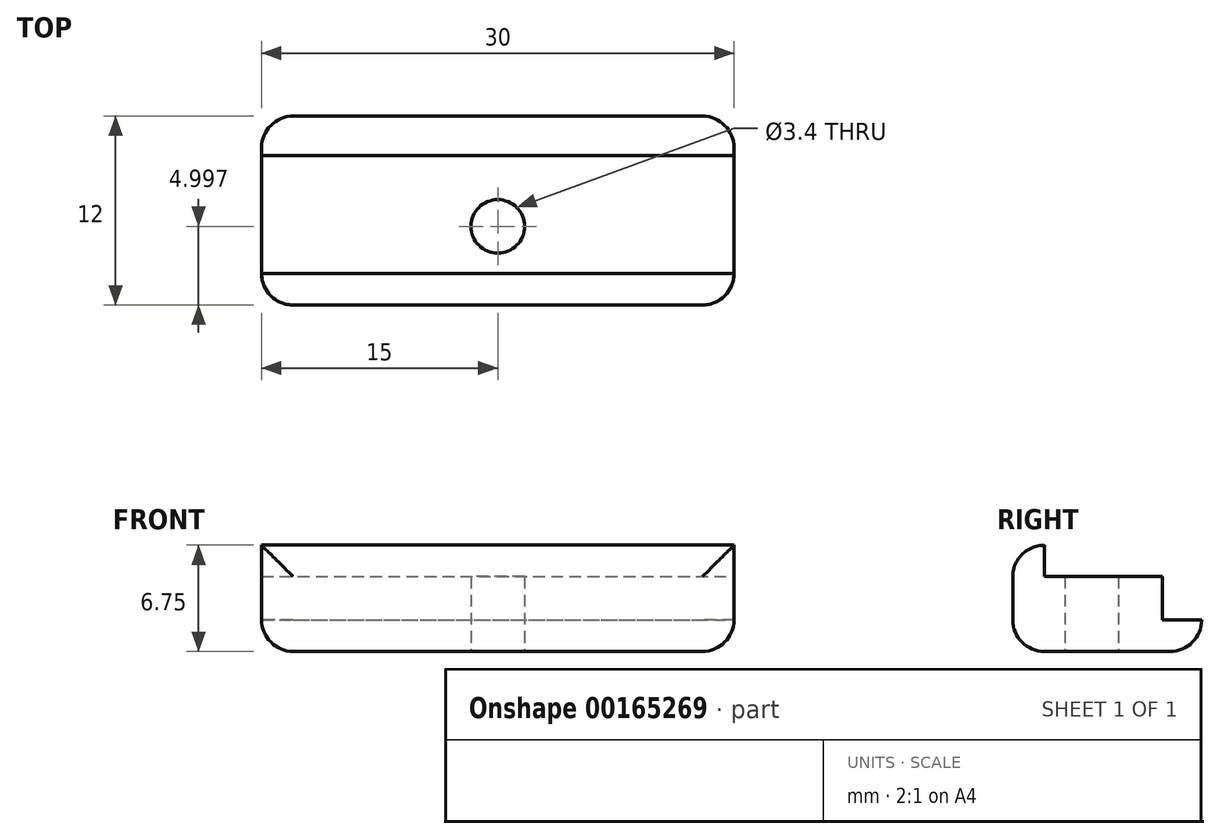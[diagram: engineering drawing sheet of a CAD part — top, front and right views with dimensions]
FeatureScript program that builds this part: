
annotation { "Feature Type Name" : "Feature", "Feature Type Description" : "" }
export const myFeature = defineFeature(function(context is Context, id is Id, definition is map)
    precondition{}
    {
        {
            var Q0;
            Q0=qCreatedBy(makeId("Top.planeOp"),FACE);
            var sketch = newSketch(context, id + "F0", { "sketchPlane" : qUnion([Q0])});
            skLineSegment(sketch, "E0.bottom", {"start": v(-7.16, 2.14) * mm, "end": v(22.84, 2.14) * mm});
            skLineSegment(sketch, "E0.top", {"start": v(-7.16, -9.86) * mm, "end": v(22.84, -9.86) * mm});
            skLineSegment(sketch, "E0.left", {"start": v(-7.16, 2.14) * mm, "end": v(-7.16, -9.86) * mm});
            skLineSegment(sketch, "E0.right", {"start": v(22.84, 2.14) * mm, "end": v(22.84, -9.86) * mm});
            skLineSegment(sketch, "E1.top", {"start": v(-7.16, -0.36) * mm, "end": v(22.84, -0.36) * mm});
            skLineSegment(sketch, "E1.left", {"start": v(-7.16, -9.86) * mm, "end": v(-7.16, -0.36) * mm});
            skLineSegment(sketch, "E1.right", {"start": v(22.84, -9.86) * mm, "end": v(22.84, -0.36) * mm});
            skLineSegment(sketch, "E2.top", {"start": v(-7.16, -7.86) * mm, "end": v(22.84, -7.86) * mm});
            skLineSegment(sketch, "E2.left", {"start": v(-7.16, -9.86) * mm, "end": v(-7.16, -7.86) * mm});
            skLineSegment(sketch, "E2.right", {"start": v(22.84, -9.86) * mm, "end": v(22.84, -7.86) * mm});
            skCircle(sketch, "E3", {"center": v(7.84, -4.86) * mm, "radius": 1.7 * mm});
            skPoint(sketch, "E3.centerSnap0", {"position": v(7.84, -7.86) * mm});
            skSolve(sketch);
        }
        {
            var Q0;
            Q0=makeQuery(id+"F0.imprint","IMPRINT",FACE,{"disambiguationData":[TD([[makeQuery(id+"F0.imprint","IMPRINT",EDGE,{"derivedFrom":sQuery(id+"F0.wireOp",EDGE,"E0.bottom")}),-1.0]])]});
            extrude(context, id + "F1", {"entities" : qUnion([Q0]), "depth" : 2 * mm});
        }
        {
            var Q0;
            Q0=makeQuery(id+"F0.imprint","IMPRINT",FACE,{"disambiguationData":[TD([[makeQuery(id+"F0.imprint","IMPRINT",EDGE,{"derivedFrom":sQuery(id+"F0.wireOp",EDGE,"E1.top")}),-1.0]])]});
            extrude(context, id + "F2", {"entities" : qUnion([Q0]), "operationType" : NewBodyOperationType.ADD, "depth" : 4.75 * mm});
        }
        {
            var Q0;
            Q0=makeQuery(id+"F0.imprint","IMPRINT",FACE,{"disambiguationData":[TD([[makeQuery(id+"F0.imprint","IMPRINT",EDGE,{"derivedFrom":sQuery(id+"F0.wireOp",EDGE,"E0.top")}),1.0]])]});
            extrude(context, id + "F3", {"entities" : qUnion([Q0]), "operationType" : NewBodyOperationType.ADD, "depth" : 6.75 * mm});
        }
        {
            var Q0;
            Q0=makeQuery(id+"F1.opExtrude","SWEPT_EDGE",EDGE,{"disambiguationData":[OSD([sQuery(id+"F0.wireOp",EDGE,"E0.bottom"),sQuery(id+"F0.wireOp",EDGE,"E0.left")])]});
            var Q1;
            Q1=makeQuery(id+"F1.opExtrude","SWEPT_EDGE",EDGE,{"disambiguationData":[OSD([sQuery(id+"F0.wireOp",EDGE,"E0.bottom"),sQuery(id+"F0.wireOp",EDGE,"E0.right")])]});
            var Q2;
            Q2=makeQuery(id+"F3.opExtrude","SWEPT_EDGE",EDGE,{"disambiguationData":[OSD([sQuery(id+"F0.wireOp",EDGE,"E0.top"),sQuery(id+"F0.wireOp",EDGE,"E2.left")])]});
            var Q3;
            Q3=makeQuery(id+"F3.opExtrude","SWEPT_EDGE",EDGE,{"disambiguationData":[OSD([sQuery(id+"F0.wireOp",EDGE,"E0.top"),sQuery(id+"F0.wireOp",EDGE,"E2.right")])]});
            var Q4;
            Q4=makeQuery(id+"F1.opExtrude","CAP_EDGE",EDGE,{"disambiguationData":[OSD([sQuery(id+"F0.wireOp",EDGE,"E0.bottom")])],"isStart":true});
            var Q5;
            Q5=makeQuery(id+"F3.boolean.opBoolean","MERGE",EDGE,{"derivedFrom":[makeQuery(id+"F2.boolean.opBoolean","MERGE",EDGE,{"derivedFrom":[makeQuery(id+"F1.opExtrude","CAP_EDGE",EDGE,{"disambiguationData":[OSD([sQuery(id+"F0.wireOp",EDGE,"E0.right")])],"isStart":true}),makeQuery(id+"F2.opExtrude","CAP_EDGE",EDGE,{"disambiguationData":[OSD([sQuery(id+"F0.wireOp",EDGE,"E1.right")])],"isStart":true})]}),makeQuery(id+"F3.opExtrude","CAP_EDGE",EDGE,{"disambiguationData":[OSD([sQuery(id+"F0.wireOp",EDGE,"E2.right")])],"isStart":true})]});
            var Q6;
            Q6=makeQuery(id+"F3.boolean.opBoolean","MERGE",EDGE,{"derivedFrom":[makeQuery(id+"F2.boolean.opBoolean","MERGE",EDGE,{"derivedFrom":[makeQuery(id+"F1.opExtrude","CAP_EDGE",EDGE,{"disambiguationData":[OSD([sQuery(id+"F0.wireOp",EDGE,"E0.left")])],"isStart":true}),makeQuery(id+"F2.opExtrude","CAP_EDGE",EDGE,{"disambiguationData":[OSD([sQuery(id+"F0.wireOp",EDGE,"E1.left")])],"isStart":true})]}),makeQuery(id+"F3.opExtrude","CAP_EDGE",EDGE,{"disambiguationData":[OSD([sQuery(id+"F0.wireOp",EDGE,"E2.left")])],"isStart":true})]});
            var Q7;
            Q7=makeQuery(id+"F3.opExtrude","CAP_EDGE",EDGE,{"disambiguationData":[OSD([sQuery(id+"F0.wireOp",EDGE,"E0.top")])],"isStart":true});
            var Q8;
            Q8=makeQuery(id+"F3.opExtrude","CAP_EDGE",EDGE,{"disambiguationData":[OSD([sQuery(id+"F0.wireOp",EDGE,"E0.top")])],"isStart":false});
            fillet(context, id + "F4", {"entities" : qUnion([Q0, Q1, Q2, Q3, Q4, Q5, Q6, Q7, Q8]), "radius" : 2 * mm, "tangentPropagation" : true, "allowEdgeOverflow" : false});
        }
    });
